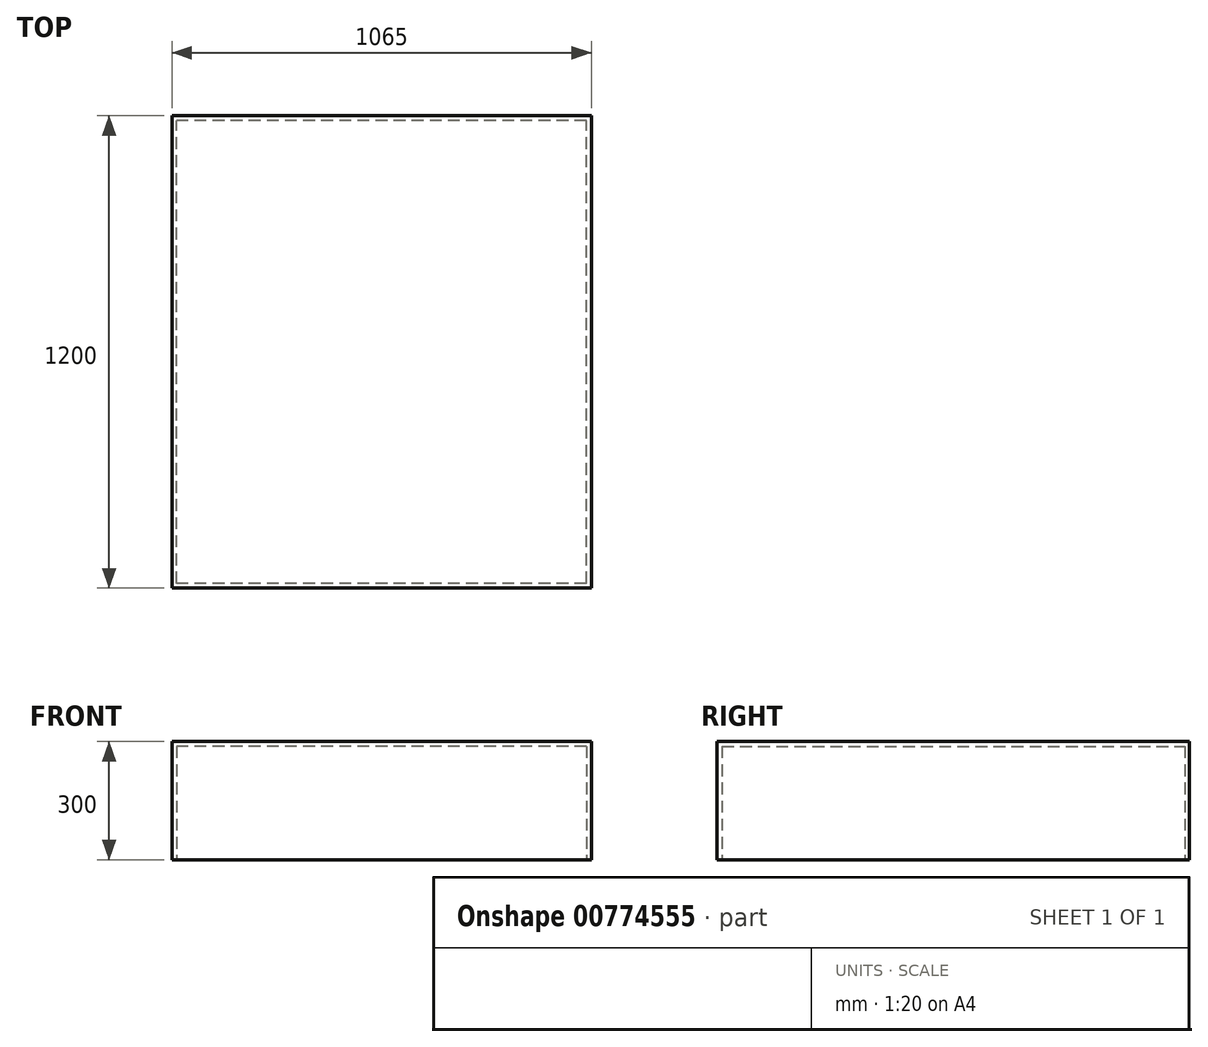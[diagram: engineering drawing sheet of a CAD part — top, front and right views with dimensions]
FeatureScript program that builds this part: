
annotation { "Feature Type Name" : "Feature", "Feature Type Description" : "" }
export const myFeature = defineFeature(function(context is Context, id is Id, definition is map)
    precondition{}
    {
        {
            var Q0;
            Q0=qCreatedBy(makeId("Top.planeOp"),FACE);
            var sketch = newSketch(context, id + "F0", { "sketchPlane" : qUnion([Q0])});
            skLineSegment(sketch, "E0.bottom", {"start": v(532.5, -600) * mm, "end": v(-532.5, -600) * mm});
            skLineSegment(sketch, "E0.top", {"start": v(532.5, 600) * mm, "end": v(-532.5, 600) * mm});
            skLineSegment(sketch, "E0.left", {"start": v(532.5, -600) * mm, "end": v(532.5, 600) * mm});
            skLineSegment(sketch, "E0.right", {"start": v(-532.5, -600) * mm, "end": v(-532.5, 600) * mm});
            skPoint(sketch, "E0.middle", {"position": v(0, 0) * mm});
            skLineSegment(sketch, "E1.bottom", {"start": v(520.5, -588) * mm, "end": v(-520.5, -588) * mm});
            skLineSegment(sketch, "E1.top", {"start": v(520.5, 588) * mm, "end": v(-520.5, 588) * mm});
            skLineSegment(sketch, "E1.left", {"start": v(520.5, -588) * mm, "end": v(520.5, 588) * mm});
            skLineSegment(sketch, "E1.right", {"start": v(-520.5, -588) * mm, "end": v(-520.5, 588) * mm});
            skSolve(sketch);
        }
        {
            var Q0;
            Q0 = qSketchRegion(id + "F0", true);
            extrude(context, id + "F1", {"entities" : qUnion([Q0]), "depth" : 300 * mm, "offsetDistance" : 25 * mm});
        }
        {
            var Q0;
            Q0=makeQuery(id+"F1.opExtrude","CAP_FACE",FACE,{"disambiguationData":[OSD([sQuery(id+"F0.wireOp",EDGE,"E0.bottom"),sQuery(id+"F0.wireOp",EDGE,"E0.top"),sQuery(id+"F0.wireOp",EDGE,"E0.left"),sQuery(id+"F0.wireOp",EDGE,"E0.right"),sQuery(id+"F0.wireOp",EDGE,"E1.bottom"),sQuery(id+"F0.wireOp",EDGE,"E1.top"),sQuery(id+"F0.wireOp",EDGE,"E1.left"),sQuery(id+"F0.wireOp",EDGE,"E1.right")])],"isStart":false});
            var sketch = newSketch(context, id + "F2", { "sketchPlane" : qUnion([Q0])});
            skLineSegment(sketch, "E2.bottom", {"start": v(-532.5, 600) * mm, "end": v(532.5, 600) * mm});
            skLineSegment(sketch, "E2.top", {"start": v(-532.5, -600) * mm, "end": v(532.5, -600) * mm});
            skLineSegment(sketch, "E2.left", {"start": v(-532.5, 600) * mm, "end": v(-532.5, -600) * mm});
            skLineSegment(sketch, "E2.right", {"start": v(532.5, 600) * mm, "end": v(532.5, -600) * mm});
            skPoint(sketch, "E2.middle", {"position": v(0, 0) * mm});
            skSolve(sketch);
        }
        {
            var Q0;
            Q0 = qSketchRegion(id + "F2", true);
            extrude(context, id + "F3", {"entities" : qUnion([Q0]), "operationType" : NewBodyOperationType.ADD, "oppositeDirection" : true, "depth" : 12 * mm, "offsetDistance" : 25 * mm});
        }
    });
